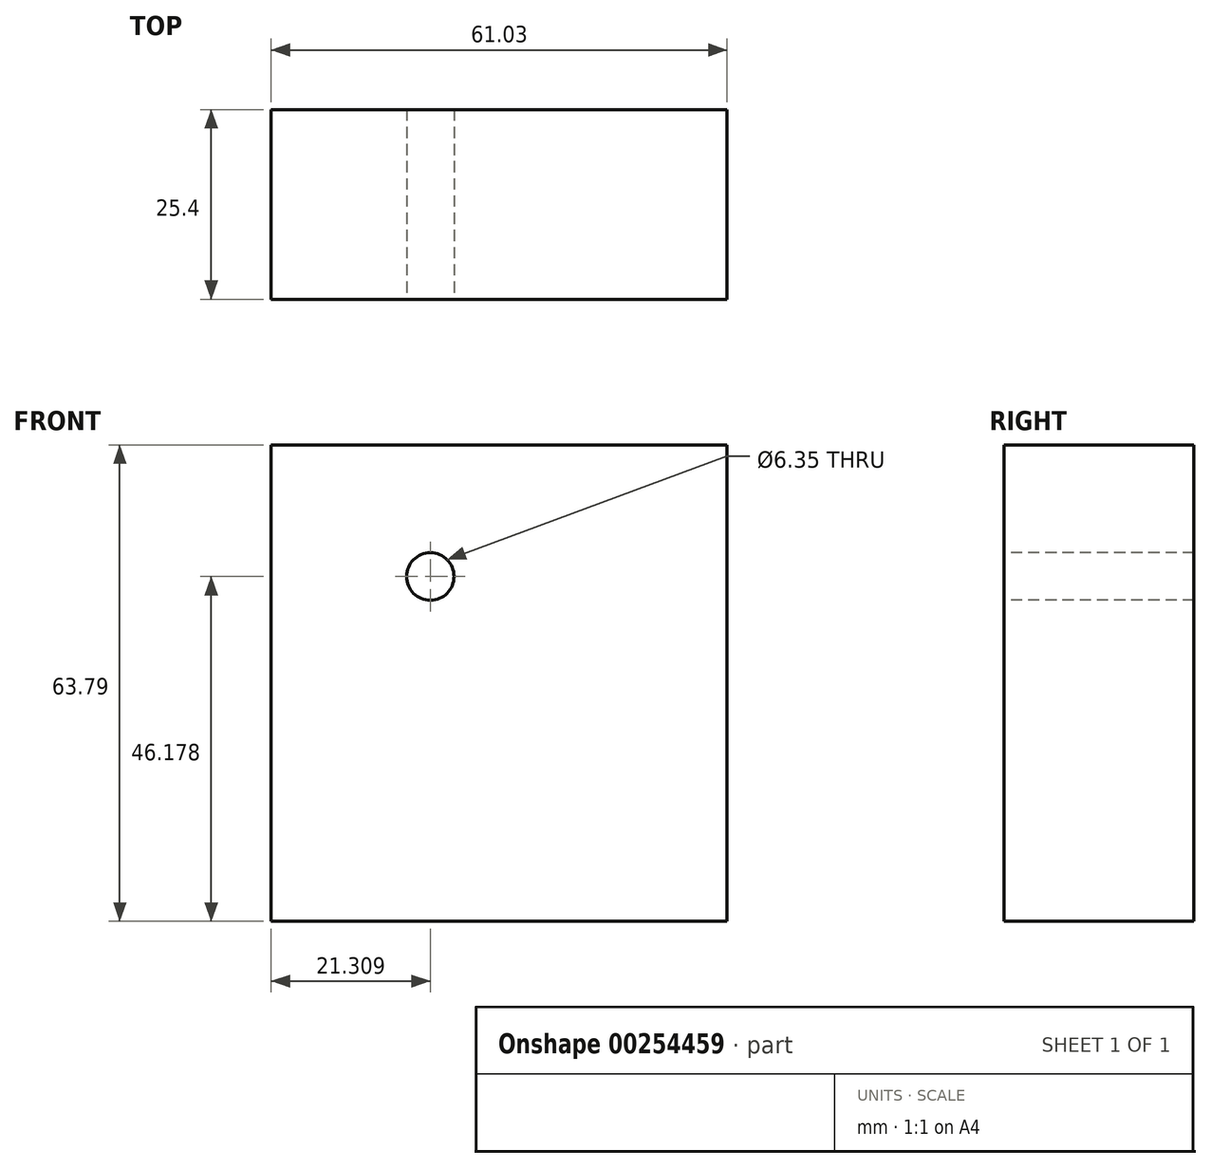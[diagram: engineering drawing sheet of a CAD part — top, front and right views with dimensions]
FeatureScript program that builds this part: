
annotation { "Feature Type Name" : "Feature", "Feature Type Description" : "" }
export const myFeature = defineFeature(function(context is Context, id is Id, definition is map)
    precondition{}
    {
        {
            var Q0;
            Q0=qCreatedBy(makeId("Front.planeOp"),FACE);
            var sketch = newSketch(context, id + "F0", { "sketchPlane" : qUnion([Q0])});
            skLineSegment(sketch, "E0.bottom", {"start": v(-32.82, 34.66) * mm, "end": v(28.2, 34.66) * mm});
            skLineSegment(sketch, "E0.top", {"start": v(-32.82, -29.13) * mm, "end": v(28.2, -29.13) * mm});
            skLineSegment(sketch, "E0.left", {"start": v(-32.82, 34.66) * mm, "end": v(-32.82, -29.13) * mm});
            skLineSegment(sketch, "E0.right", {"start": v(28.2, 34.66) * mm, "end": v(28.2, -29.13) * mm});
            skSolve(sketch);
        }
        {
            var Q0;
            Q0=makeQuery(id+"F0.imprint","IMPRINT",FACE,{"disambiguationData":[TD([[makeQuery(id+"F0.imprint","IMPRINT",EDGE,{"derivedFrom":sQuery(id+"F0.wireOp",EDGE,"E0.bottom")}),-1.0]])]});
            extrude(context, id + "F1", {"entities" : qUnion([Q0]), "depth" : 25.4 * mm});
        }
        {
            var Q0;
            Q0=makeQuery(id+"F1.opExtrude","CAP_FACE",FACE,{"disambiguationData":[OSD([sQuery(id+"F0.wireOp",EDGE,"E0.bottom"),sQuery(id+"F0.wireOp",EDGE,"E0.top"),sQuery(id+"F0.wireOp",EDGE,"E0.left"),sQuery(id+"F0.wireOp",EDGE,"E0.right")])],"isStart":false});
            var sketch = newSketch(context, id + "F2", { "sketchPlane" : qUnion([Q0])});
            skPoint(sketch, "E1", {"position": v(-11.51, 17.05) * mm});
            skSolve(sketch);
        }
        {
            var Q0;
            Q0=sQuery(id+"F2.wireOp",VERTEX,"E1");
            var Q1;
            Q1=makeQuery(id+"F1.opExtrude","SWEPT_BODY",BODY,{"disambiguationData":[OSD([sQuery(id+"F0.wireOp",EDGE,"E0.bottom"),sQuery(id+"F0.wireOp",EDGE,"E0.top"),sQuery(id+"F0.wireOp",EDGE,"E0.left"),sQuery(id+"F0.wireOp",EDGE,"E0.right")])]});
            hole(context, id + "F3", {"style" : HoleStyle.SIMPLE, "endStyle" : HoleEndStyle.THROUGH, "holeDiameter" : 6.35 * mm, "tappedDepth" : 12.7 * mm, "tapClearance" : 3, "locations" : qUnion([Q0]), "scope" : qUnion([Q1])});
        }
    });
